# Revit family: Seating-Solo_Lounge_Chair-Teknion-Zones_ZNSXL-R2013
name_source: partatom
category: Furniture
revit_build: Autodesk Revit 2013 (Build: 20130531_2115(x64)
units: mm (PartAtom-declared; Revit-internal decimal feet)

## types (2) — shared parameters
Assembly Code = E2020200
Depth = 31 5/8"
Height = 32 3/8"
Manufacturer = Teknion
Manufacturer Fax = 416.661.4586
Part Number = ZNSXL
Product Documentation Link = http://www.teknion.com
Product Line = Zones
Product Page URL = http://www.teknion.com
Series = Zones
Sustainability Data = http://www.teknion.com
URL = http://www.teknion.com
Warranty = http://www.teknion.com
Width = 25 1/2"

## per-type parameters (varying)
| type | Description | Model | With Metal Loop Arms |
| Solo Lounge Chair With Arms | Zones Solo Lounge Chair, Low-Wide Back, With Metal Loop Arms | ZNSXLA | Yes |
| Solo Lounge Chair | Zones Solo Lounge Chair, Low-Wide Back, No Arms
Zones Solo Lounge Chair, Low-Wide Back, No Arms
Zones Solo Lounge Chair, Low-Wide Back, No Arms | ZNSXLN | No |

## geometry (parser evidence)
native form markers: Blend x679, Sweep x5
no freeform markers — native parametric forms only
